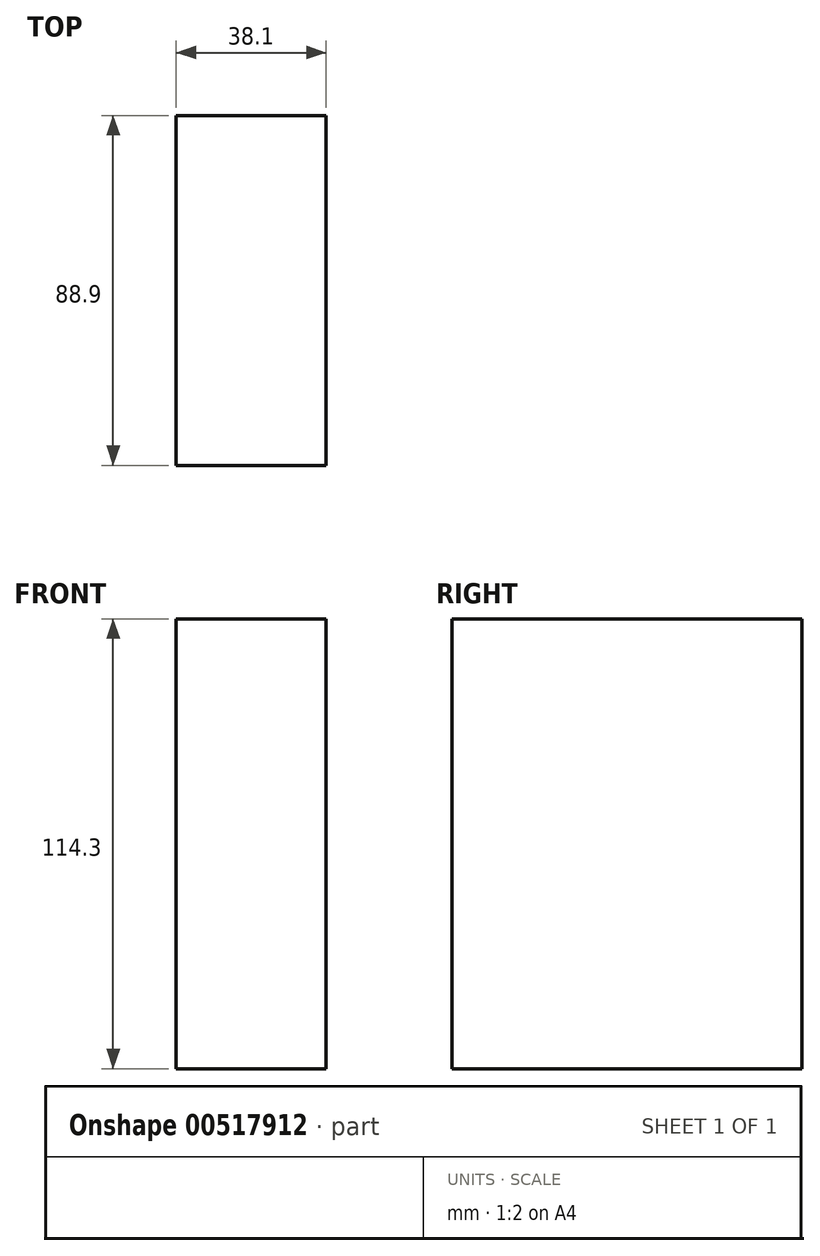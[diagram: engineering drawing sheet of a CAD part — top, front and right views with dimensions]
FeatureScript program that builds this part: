
annotation { "Feature Type Name" : "Feature", "Feature Type Description" : "" }
export const myFeature = defineFeature(function(context is Context, id is Id, definition is map)
    precondition{}
    {
        {
            var Q0;
            Q0=qCreatedBy(makeId("Top.planeOp"),FACE);
            var sketch = newSketch(context, id + "F0", { "sketchPlane" : qUnion([Q0])});
            skLineSegment(sketch, "E0.bottom", {"start": v(19.05, 44.45) * mm, "end": v(-19.05, 44.45) * mm});
            skLineSegment(sketch, "E0.top", {"start": v(19.05, -44.45) * mm, "end": v(-19.05, -44.45) * mm});
            skLineSegment(sketch, "E0.left", {"start": v(19.05, 44.45) * mm, "end": v(19.05, -44.45) * mm});
            skLineSegment(sketch, "E0.right", {"start": v(-19.05, 44.45) * mm, "end": v(-19.05, -44.45) * mm});
            skPoint(sketch, "E0.middle", {"position": v(0, 0) * mm});
            skSolve(sketch);
        }
        {
            var Q0;
            Q0=makeQuery(id+"F0.imprint","IMPRINT",FACE,{"disambiguationData":[TD([[makeQuery(id+"F0.imprint","IMPRINT",EDGE,{"derivedFrom":sQuery(id+"F0.wireOp",EDGE,"E0.bottom")}),1.0]])]});
            extrude(context, id + "F1", {"entities" : qUnion([Q0]), "endBound" : BoundingType.SYMMETRIC, "depth" : 114.3 * mm, "offsetDistance" : 25.4 * mm});
        }
    });
